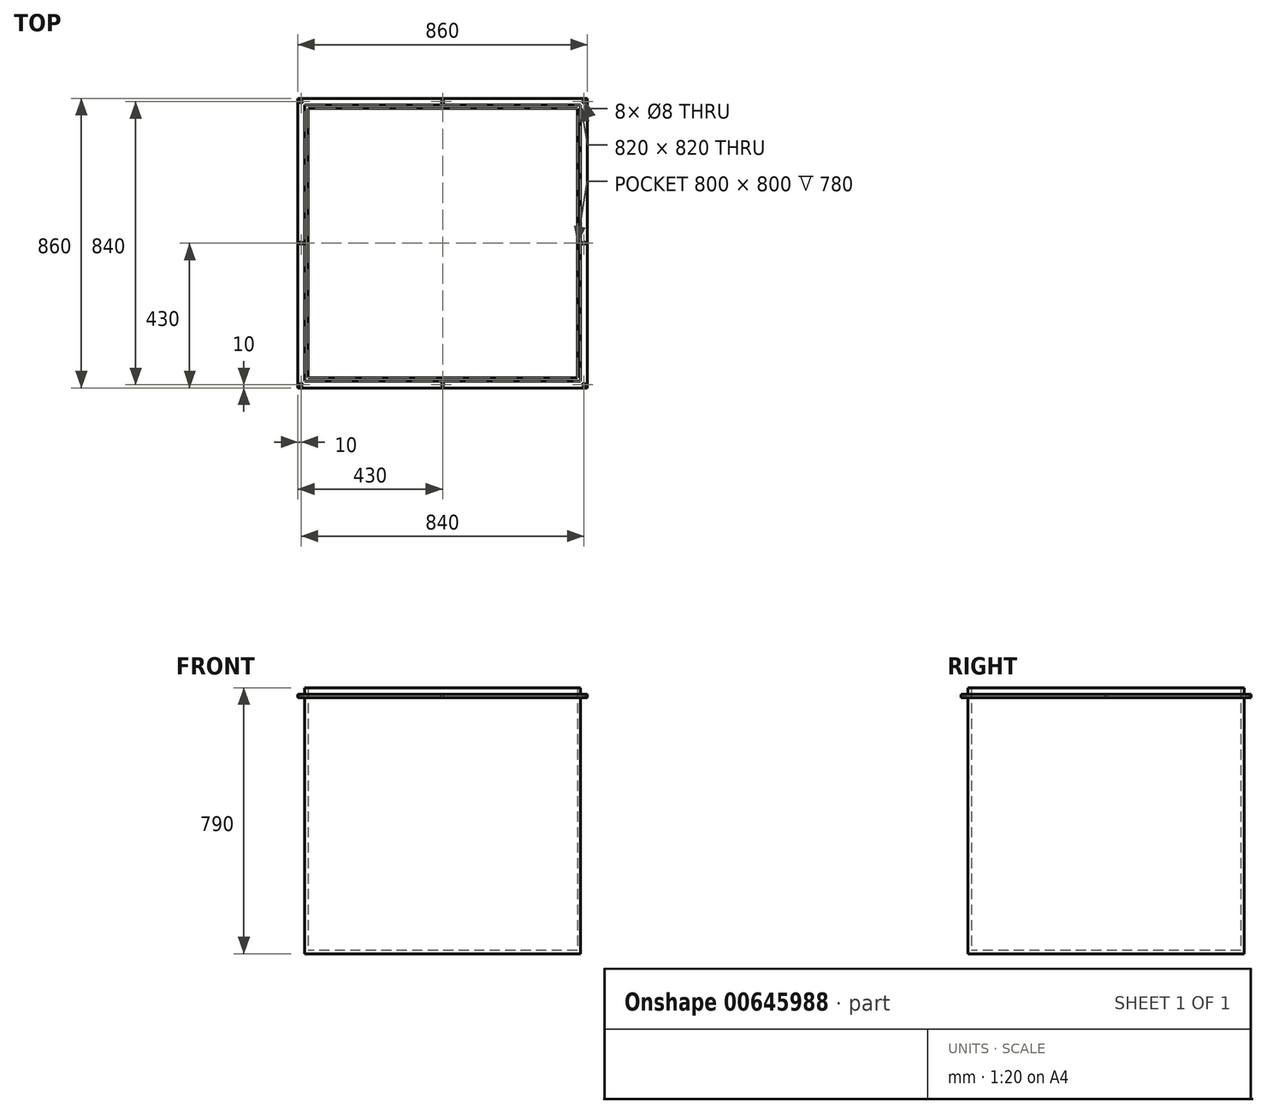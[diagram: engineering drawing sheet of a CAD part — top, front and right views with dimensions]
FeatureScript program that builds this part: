
annotation { "Feature Type Name" : "Feature", "Feature Type Description" : "" }
export const myFeature = defineFeature(function(context is Context, id is Id, definition is map)
    precondition{}
    {
        {
            var Q0;
            Q0=qCreatedBy(makeId("Top.planeOp"),FACE);
            var sketch = newSketch(context, id + "F0", { "sketchPlane" : qUnion([Q0])});
            skLineSegment(sketch, "E0.bottom", {"start": v(410, 410) * mm, "end": v(-410, 410) * mm});
            skLineSegment(sketch, "E0.top", {"start": v(410, -410) * mm, "end": v(-410, -410) * mm});
            skLineSegment(sketch, "E0.left", {"start": v(410, 410) * mm, "end": v(410, -410) * mm});
            skLineSegment(sketch, "E0.right", {"start": v(-410, 410) * mm, "end": v(-410, -410) * mm});
            skPoint(sketch, "E0.middle", {"position": v(0, 0) * mm});
            skSolve(sketch);
        }
        {
            var Q0;
            Q0 = qSketchRegion(id + "F0", true);
            extrude(context, id + "F1", {"entities" : qUnion([Q0]), "depth" : 790 * mm, "offsetDistance" : 25 * mm});
        }
        {
            var Q0;
            Q0=makeQuery(id+"F1.opExtrude","CAP_FACE",FACE,{"disambiguationData":[OSD([sQuery(id+"F0.wireOp",EDGE,"E0.bottom"),sQuery(id+"F0.wireOp",EDGE,"E0.top"),sQuery(id+"F0.wireOp",EDGE,"E0.left"),sQuery(id+"F0.wireOp",EDGE,"E0.right")])],"isStart":false});
            shell(context, id + "F2", {"entities" : qUnion([Q0]), "thickness" : 10 * mm});
        }
        {
            var Q0;
            Q0=makeQuery(id+"F1.opExtrude","CAP_FACE",FACE,{"disambiguationData":[OSD([sQuery(id+"F0.wireOp",EDGE,"E0.bottom"),sQuery(id+"F0.wireOp",EDGE,"E0.top"),sQuery(id+"F0.wireOp",EDGE,"E0.left"),sQuery(id+"F0.wireOp",EDGE,"E0.right")])],"isStart":false});
            cPlane(context, id + "F3", {"entities" : qUnion([Q0]), "cplaneType" : CPlaneType.OFFSET, "offset" : 20 * mm, "oppositeDirection" : true, "width" : 150 * mm, "height" : 150 * mm});
        }
        {
            var Q0;
            Q0=qCreatedBy(id+"F3.planeOp",FACE);
            var sketch = newSketch(context, id + "F4", { "sketchPlane" : qUnion([Q0])});
            skLineSegment(sketch, "E1.bottom", {"start": v(-430, 430) * mm, "end": v(430, 430) * mm});
            skLineSegment(sketch, "E1.top", {"start": v(-430, -430) * mm, "end": v(430, -430) * mm});
            skLineSegment(sketch, "E1.left", {"start": v(-430, 430) * mm, "end": v(-430, -430) * mm});
            skLineSegment(sketch, "E1.right", {"start": v(430, 430) * mm, "end": v(430, -430) * mm});
            skPoint(sketch, "E1.middle", {"position": v(0, 0) * mm});
            skLineSegment(sketch, "E2.0", {"start": v(-410, 410) * mm, "end": v(-410, -410) * mm});
            skLineSegment(sketch, "E3.0", {"start": v(410, 410) * mm, "end": v(-410, 410) * mm});
            skLineSegment(sketch, "E4.0", {"start": v(410, 410) * mm, "end": v(410, -410) * mm});
            skLineSegment(sketch, "E5.0", {"start": v(410, -410) * mm, "end": v(-410, -410) * mm});
            skSolve(sketch);
        }
        {
            var Q0;
            Q0=makeQuery(id+"F4.imprint","IMPRINT",FACE,{"disambiguationData":[TD([[makeQuery(id+"F4.imprint","IMPRINT",EDGE,{"derivedFrom":sQuery(id+"F4.wireOp",EDGE,"E1.bottom")}),-1.0]])]});
            extrude(context, id + "F5", {"entities" : qUnion([Q0]), "operationType" : NewBodyOperationType.ADD, "oppositeDirection" : true, "depth" : 10 * mm, "offsetDistance" : 25 * mm});
        }
        {
            var Q0;
            Q0=makeQuery(id+"F5.opExtrude","CAP_FACE",FACE,{"disambiguationData":[OSD([sQuery(id+"F4.wireOp",EDGE,"E1.bottom"),sQuery(id+"F4.wireOp",EDGE,"E1.top"),sQuery(id+"F4.wireOp",EDGE,"E1.left"),sQuery(id+"F4.wireOp",EDGE,"E1.right"),sQuery(id+"F4.wireOp",EDGE,"E2.0"),sQuery(id+"F4.wireOp",EDGE,"E3.0"),sQuery(id+"F4.wireOp",EDGE,"E4.0"),sQuery(id+"F4.wireOp",EDGE,"E5.0")])],"isStart":true});
            var sketch = newSketch(context, id + "F6", { "sketchPlane" : qUnion([Q0])});
            skLineSegment(sketch, "E6.bottom", {"start": v(-420, 420) * mm, "end": v(420, 420) * mm});
            skLineSegment(sketch, "E6.top", {"start": v(-420, -420) * mm, "end": v(420, -420) * mm});
            skLineSegment(sketch, "E6.left", {"start": v(-420, 420) * mm, "end": v(-420, -420) * mm});
            skLineSegment(sketch, "E6.right", {"start": v(420, 420) * mm, "end": v(420, -420) * mm});
            skPoint(sketch, "E6.middle", {"position": v(0, 0) * mm});
            skPoint(sketch, "E7", {"position": v(-420, 420) * mm});
            skPoint(sketch, "E8", {"position": v(420, 420) * mm});
            skPoint(sketch, "E9", {"position": v(420, -420) * mm});
            skPoint(sketch, "E10", {"position": v(-420, -420) * mm});
            skPoint(sketch, "E11", {"position": v(0, -420) * mm});
            skPoint(sketch, "E12", {"position": v(420, 0) * mm});
            skPoint(sketch, "E13", {"position": v(-420, 0) * mm});
            skPoint(sketch, "E14", {"position": v(0, 420) * mm});
            skSolve(sketch);
        }
        {
            var Q0;
            Q0=sQuery(id+"F6.wireOp",VERTEX,"E14");
            var Q1;
            Q1=sQuery(id+"F6.wireOp",VERTEX,"E7");
            var Q2;
            Q2=sQuery(id+"F6.wireOp",VERTEX,"E13");
            var Q3;
            Q3=sQuery(id+"F6.wireOp",VERTEX,"E10");
            var Q4;
            Q4=sQuery(id+"F6.wireOp",VERTEX,"E11");
            var Q5;
            Q5=sQuery(id+"F6.wireOp",VERTEX,"E12");
            var Q6;
            Q6=sQuery(id+"F6.wireOp",VERTEX,"E9");
            var Q7;
            Q7=sQuery(id+"F6.wireOp",VERTEX,"E8");
            var Q8;
            Q8=makeQuery(id+"F1.opExtrude","SWEPT_BODY",BODY,{"disambiguationData":[OSD([sQuery(id+"F0.wireOp",EDGE,"E0.bottom"),sQuery(id+"F0.wireOp",EDGE,"E0.top"),sQuery(id+"F0.wireOp",EDGE,"E0.left"),sQuery(id+"F0.wireOp",EDGE,"E0.right")])]});
            hole(context, id + "F7", {"style" : HoleStyle.SIMPLE, "endStyle" : HoleEndStyle.THROUGH, "holeDiameter" : 8 * mm, "majorDiameter" : 5 * mm, "isTappedThrough" : true, "tappedDepth" : 12 * mm, "tapClearance" : 3, "locations" : qUnion([Q0, Q1, Q2, Q3, Q4, Q5, Q6, Q7]), "scope" : qUnion([Q8])});
        }
    });
